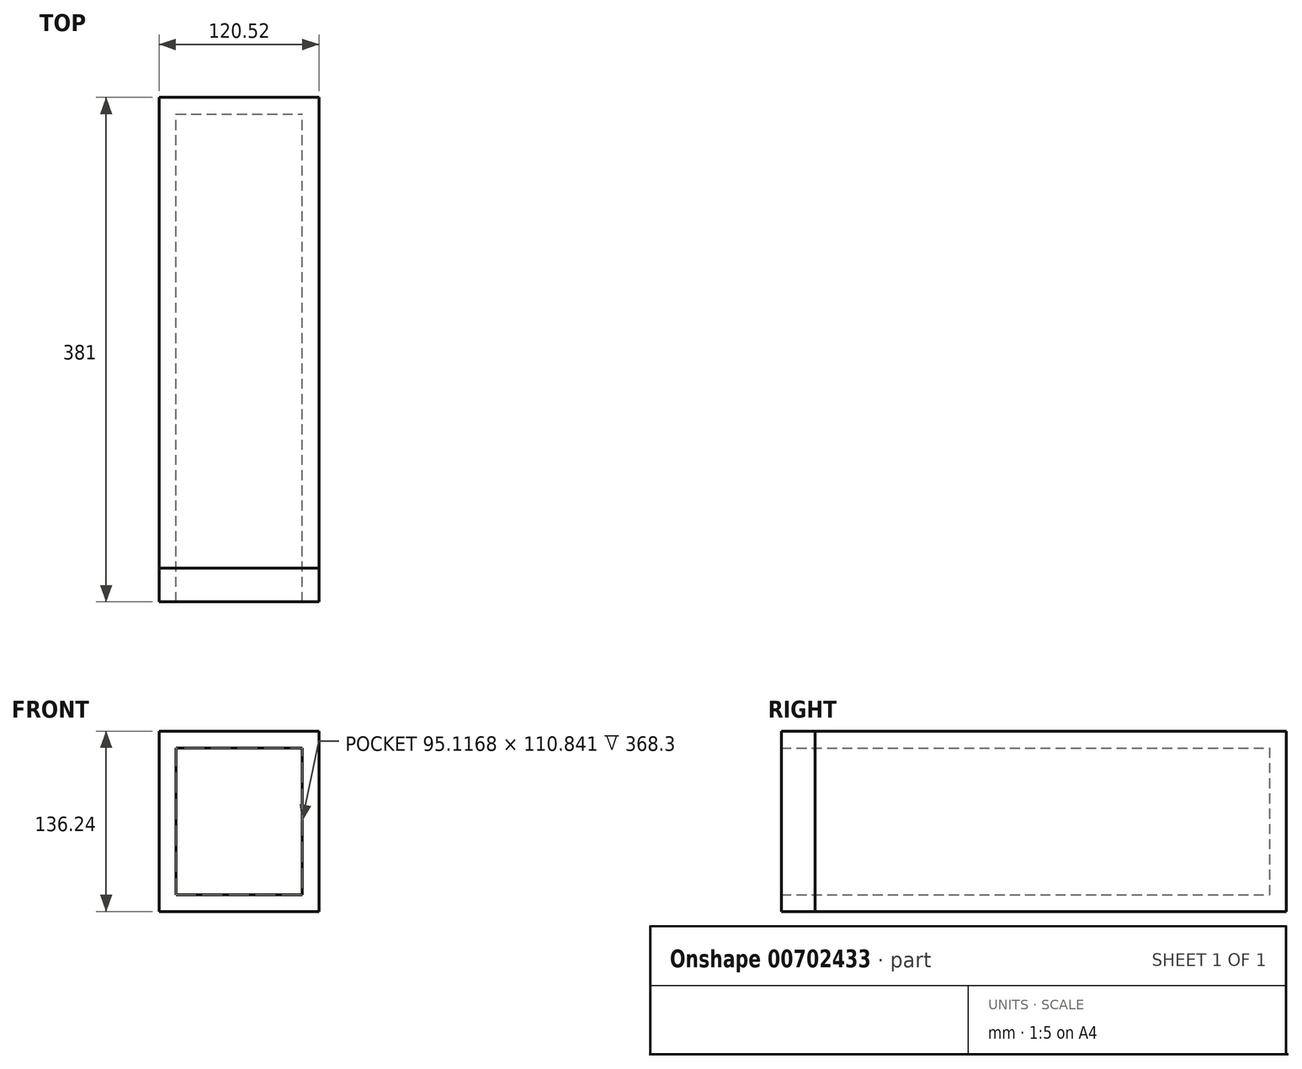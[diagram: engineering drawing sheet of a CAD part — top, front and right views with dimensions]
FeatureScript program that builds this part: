
annotation { "Feature Type Name" : "Feature", "Feature Type Description" : "" }
export const myFeature = defineFeature(function(context is Context, id is Id, definition is map)
    precondition{}
    {
        {
            var Q0;
            Q0=qCreatedBy(makeId("Front.planeOp"),FACE);
            var sketch = newSketch(context, id + "F0", { "sketchPlane" : qUnion([Q0])});
            skLineSegment(sketch, "E0.bottom", {"start": v(-72.32, 68.96) * mm, "end": v(22.8, 68.96) * mm});
            skLineSegment(sketch, "E0.top", {"start": v(-72.32, -67.28) * mm, "end": v(22.8, -67.28) * mm});
            skLineSegment(sketch, "E0.left", {"start": v(-72.32, 68.96) * mm, "end": v(-72.32, -67.28) * mm});
            skLineSegment(sketch, "E0.right", {"start": v(22.8, 68.96) * mm, "end": v(22.8, -67.28) * mm});
            skSolve(sketch);
        }
        {
            var Q0;
            Q0=makeQuery(id+"F0.imprint","IMPRINT",FACE,{"disambiguationData":[TD([[makeQuery(id+"F0.imprint","IMPRINT",EDGE,{"derivedFrom":sQuery(id+"F0.wireOp",EDGE,"E0.bottom")}),-1.0]])]});
            extrude(context, id + "F1", {"entities" : qUnion([Q0]), "depth" : 381 * mm, "offsetDistance" : 25.4 * mm});
        }
        {
            var Q0;
            Q0=makeQuery(id+"F1.opExtrude","SWEPT_FACE",FACE,{"disambiguationData":[OSD([sQuery(id+"F0.wireOp",EDGE,"E0.left")])]});
            extrude(context, id + "F2", {"entities" : qUnion([Q0]), "operationType" : NewBodyOperationType.ADD, "depth" : 25.4 * mm, "offsetDistance" : 25.4 * mm});
        }
        {
            var Q0;
            {var subQ0=sQuery(id+"F0.wireOp",EDGE,"E0.left");Q0=makeQuery(id+"F2.boolean.opBoolean","MERGE",FACE,{"derivedFrom":[makeQuery(id+"F1.opExtrude","CAP_FACE",FACE,{"disambiguationData":[OSD([sQuery(id+"F0.wireOp",EDGE,"E0.bottom"),sQuery(id+"F0.wireOp",EDGE,"E0.top"),subQ0,sQuery(id+"F0.wireOp",EDGE,"E0.right")])],"isStart":false}),makeQuery(id+"F2.opExtrude","SWEPT_FACE",FACE,{"disambiguationData":[OSD([subQ0]),TDD([makeQuery(id+"F1.opExtrude","CAP_EDGE",EDGE,{"disambiguationData":[OSD([subQ0])],"isStart":false})])]})]});}
            extrude(context, id + "F3", {"entities" : qUnion([Q0]), "oppositeDirection" : true, "depth" : 25.4 * mm, "offsetDistance" : 25.4 * mm});
        }
        {
            var Q0;
            {var subQ0=sQuery(id+"F0.wireOp",EDGE,"E0.left");Q0=makeQuery(id+"F2.boolean.opBoolean","MERGE",FACE,{"derivedFrom":[makeQuery(id+"F1.opExtrude","CAP_FACE",FACE,{"disambiguationData":[OSD([sQuery(id+"F0.wireOp",EDGE,"E0.bottom"),sQuery(id+"F0.wireOp",EDGE,"E0.top"),subQ0,sQuery(id+"F0.wireOp",EDGE,"E0.right")])],"isStart":false}),makeQuery(id+"F2.opExtrude","SWEPT_FACE",FACE,{"disambiguationData":[OSD([subQ0]),TDD([makeQuery(id+"F1.opExtrude","CAP_EDGE",EDGE,{"disambiguationData":[OSD([subQ0])],"isStart":false})])]})]});}
            shell(context, id + "F4", {"entities" : qUnion([Q0]), "thickness" : 12.7 * mm});
        }
    });
